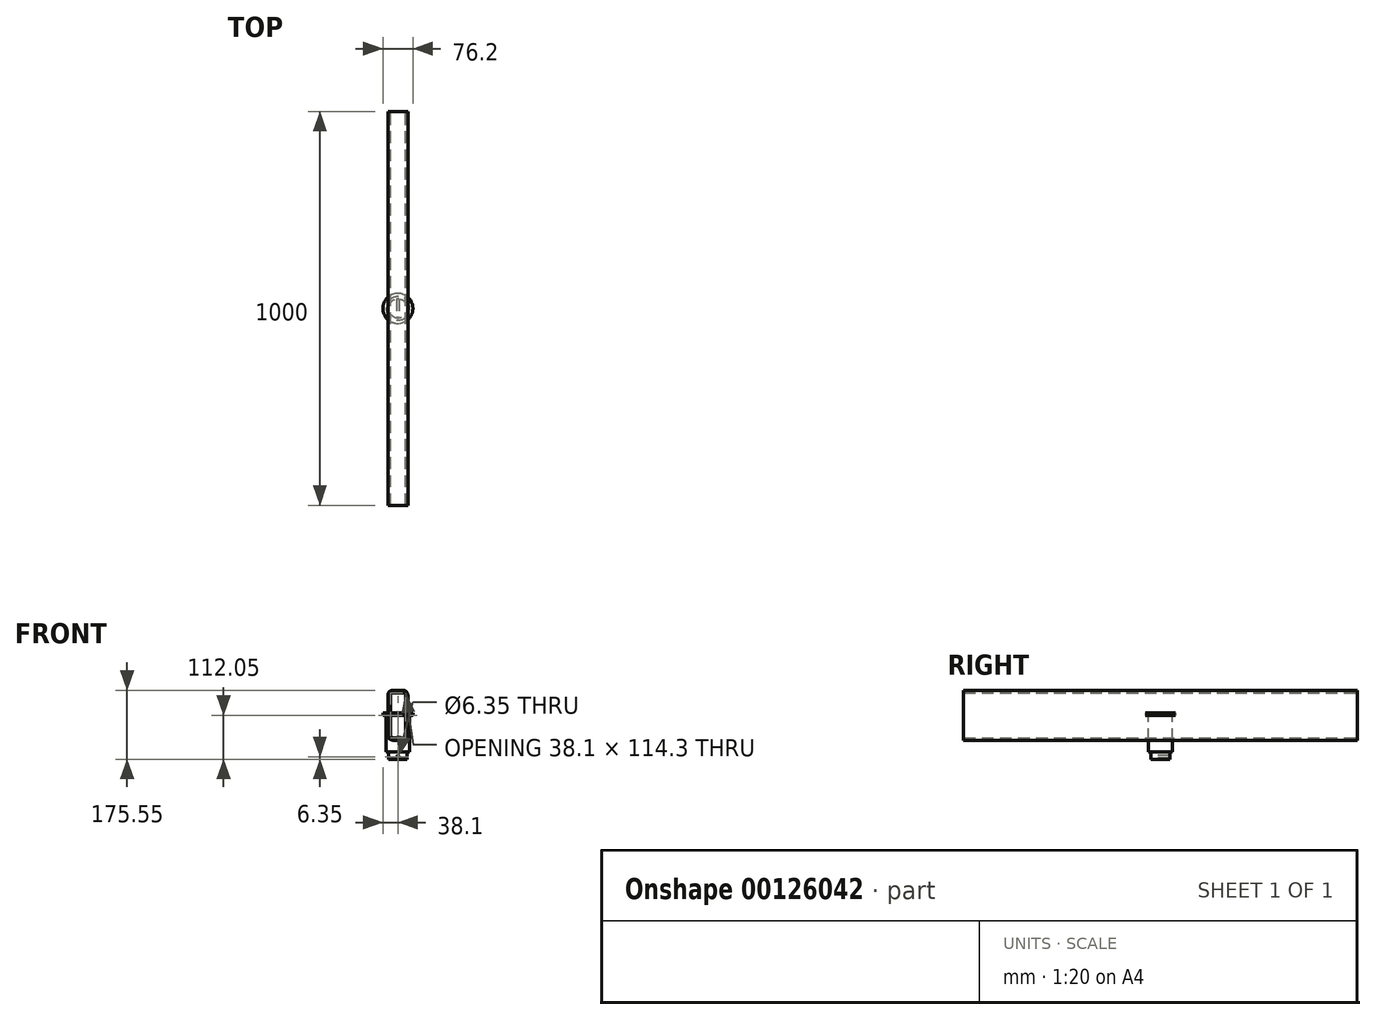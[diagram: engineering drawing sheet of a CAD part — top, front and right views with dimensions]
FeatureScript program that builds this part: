
annotation { "Feature Type Name" : "Feature", "Feature Type Description" : "" }
export const myFeature = defineFeature(function(context is Context, id is Id, definition is map)
    precondition{}
    {
        {
            var Q0;
            Q0=qCreatedBy(makeId("Top.planeOp"),FACE);
            var sketch = newSketch(context, id + "F0", { "sketchPlane" : qUnion([Q0])});
            skCircle(sketch, "E0", {"center": v(0, 0) * mm, "radius": 30 * mm});
            skSolve(sketch);
        }
        {
            var Q0;
            Q0 = qSketchRegion(id + "F0", true);
            extrude(context, id + "F1", {"entities" : qUnion([Q0]), "oppositeDirection" : true, "depth" : 93 * mm});
        }
        {
            var Q0;
            Q0=makeQuery(id+"F1.opExtrude","CAP_FACE",FACE,{"disambiguationData":[OSD([sQuery(id+"F0.wireOp",EDGE,"E0")])],"isStart":true});
            var sketch = newSketch(context, id + "F2", { "sketchPlane" : qUnion([Q0])});
            skCircle(sketch, "E1", {"center": v(0, 0) * mm, "radius": 38.1 * mm});
            skSolve(sketch);
        }
        {
            var Q0;
            Q0 = qSketchRegion(id + "F2", true);
            extrude(context, id + "F3", {"entities" : qUnion([Q0]), "operationType" : NewBodyOperationType.ADD, "depth" : 6.35 * mm});
        }
        {
            var Q0;
            Q0=makeQuery(id+"F1.opExtrude","CAP_FACE",FACE,{"disambiguationData":[OSD([sQuery(id+"F0.wireOp",EDGE,"E0")])],"isStart":false});
            var sketch = newSketch(context, id + "F4", { "sketchPlane" : qUnion([Q0])});
            skCircle(sketch, "E2", {"center": v(0, 0) * mm, "radius": 23.75 * mm});
            skSolve(sketch);
        }
        {
            var Q0;
            Q0=makeQuery(id+"F4.imprint","IMPRINT",FACE,{"disambiguationData":[TD([[makeQuery(id+"F4.imprint","IMPRINT",EDGE,{"derivedFrom":sQuery(id+"F4.wireOp",EDGE,"E2")}),1.0]])]});
            var Q1;
            Q1=sQuery(id+"F4.wireOp",EDGE,"E2");
            extrude(context, id + "F5", {"entities" : qUnion([Q0]), "surfaceEntities" : qUnion([Q1]), "depth" : 19.05 * mm});
        }
        {
            var Q0;
            Q0=qCreatedBy(makeId("Front.planeOp"),FACE);
            var sketch = newSketch(context, id + "F6", { "sketchPlane" : qUnion([Q0])});
            skCircle(sketch, "E3", {"center": v(0, -105.7) * mm, "radius": 3.17 * mm});
            skSolve(sketch);
        }
        {
            var Q0;
            Q0 = qSketchRegion(id + "F6", true);
            extrude(context, id + "F7", {"entities" : qUnion([Q0]), "operationType" : NewBodyOperationType.REMOVE, "endBound" : BoundingType.SYMMETRIC, "oppositeDirection" : true, "depth" : 60 * mm});
        }
        {
            var Q0;
            Q0=makeQuery(id+"F5.opExtrude","SWEPT_BODY",BODY,{"disambiguationData":[OSD([sQuery(id+"F4.wireOp",EDGE,"E2")])]});
            deleteBodies(context, id + "F8", {"entities" : qUnion([Q0])});
        }
        {
            var Q0;
            Q0=makeQuery(id+"F1.opExtrude","CAP_FACE",FACE,{"disambiguationData":[OSD([sQuery(id+"F0.wireOp",EDGE,"E0")])],"isStart":false});
            var sketch = newSketch(context, id + "F9", { "sketchPlane" : qUnion([Q0])});
            skCircle(sketch, "E4", {"center": v(0, 0) * mm, "radius": 23.75 * mm});
            skSolve(sketch);
        }
        {
            var Q0;
            Q0=makeQuery(id+"F9.imprint","IMPRINT",FACE,{"disambiguationData":[TD([[makeQuery(id+"F9.imprint","IMPRINT",EDGE,{"derivedFrom":sQuery(id+"F9.wireOp",EDGE,"E4")}),1.0]])]});
            extrude(context, id + "F10", {"entities" : qUnion([Q0]), "operationType" : NewBodyOperationType.ADD, "depth" : 19.05 * mm});
        }
        {
            var Q0;
            Q0=qCreatedBy(makeId("Front.planeOp"),FACE);
            var sketch = newSketch(context, id + "F11", { "sketchPlane" : qUnion([Q0])});
            skCircle(sketch, "E5", {"center": v(0, -105.7) * mm, "radius": 3.18 * mm});
            skSolve(sketch);
        }
        {
            var Q0;
            Q0 = qSketchRegion(id + "F11", true);
            extrude(context, id + "F12", {"entities" : qUnion([Q0]), "operationType" : NewBodyOperationType.REMOVE, "endBound" : BoundingType.SYMMETRIC, "oppositeDirection" : true, "depth" : 60 * mm});
        }
        {
            var Q0;
            Q0=qCreatedBy(makeId("Front.planeOp"),FACE);
            var sketch = newSketch(context, id + "F13", { "sketchPlane" : qUnion([Q0])});
            skLineSegment(sketch, "E6.bottom", {"start": v(12.7, 63.5) * mm, "end": v(-12.7, 63.5) * mm});
            skLineSegment(sketch, "E6.top", {"start": v(12.7, -63.5) * mm, "end": v(-12.7, -63.5) * mm});
            skLineSegment(sketch, "E6.left", {"start": v(25.4, 50.8) * mm, "end": v(25.4, -50.8) * mm});
            skLineSegment(sketch, "E6.right", {"start": v(-25.4, 50.8) * mm, "end": v(-25.4, -50.8) * mm});
            skPoint(sketch, "E6.middle", {"position": v(0, 0) * mm});
            skPoint(sketch, "E7.visualSharp", {"position": v(-25.4, 63.5) * mm});
            skArc(sketch, "E7.filletArc", {"start": v(-12.7, 63.5) * mm, "mid": v(-21.68, 59.78) * mm, "end": v(-25.4, 50.8) * mm});
            skPoint(sketch, "E8.visualSharp", {"position": v(25.4, 63.5) * mm});
            skArc(sketch, "E8.filletArc", {"start": v(25.4, 50.8) * mm, "mid": v(21.68, 59.78) * mm, "end": v(12.7, 63.5) * mm});
            skPoint(sketch, "E9.visualSharp", {"position": v(25.4, -63.5) * mm});
            skArc(sketch, "E9.filletArc", {"start": v(12.7, -63.5) * mm, "mid": v(21.68, -59.78) * mm, "end": v(25.4, -50.8) * mm});
            skPoint(sketch, "E10.visualSharp", {"position": v(-25.4, -63.5) * mm});
            skArc(sketch, "E10.filletArc", {"start": v(-25.4, -50.8) * mm, "mid": v(-21.68, -59.78) * mm, "end": v(-12.7, -63.5) * mm});
            skLineSegment(sketch, "E11.0", {"start": v(12.7, 57.15) * mm, "end": v(-12.7, 57.15) * mm});
            skArc(sketch, "E12.0", {"start": v(19.05, 50.8) * mm, "mid": v(17.2, 55.3) * mm, "end": v(12.7, 57.15) * mm});
            skLineSegment(sketch, "E13.0", {"start": v(19.05, 50.8) * mm, "end": v(19.05, -50.8) * mm});
            skArc(sketch, "E14.0", {"start": v(-12.7, 57.15) * mm, "mid": v(-17.2, 55.3) * mm, "end": v(-19.05, 50.8) * mm});
            skArc(sketch, "E14.1", {"start": v(12.7, -57.15) * mm, "mid": v(17.2, -55.3) * mm, "end": v(19.05, -50.8) * mm});
            skLineSegment(sketch, "E14.2", {"start": v(12.7, -57.15) * mm, "end": v(-12.7, -57.15) * mm});
            skArc(sketch, "E14.3", {"start": v(-19.05, -50.8) * mm, "mid": v(-17.2, -55.3) * mm, "end": v(-12.7, -57.15) * mm});
            skLineSegment(sketch, "E14.4", {"start": v(-19.05, 50.8) * mm, "end": v(-19.05, -50.8) * mm});
            skSolve(sketch);
        }
        {
            var Q0;
            Q0=makeQuery(id+"F13.imprint","IMPRINT",FACE,{"disambiguationData":[TD([[makeQuery(id+"F13.imprint","IMPRINT",EDGE,{"derivedFrom":sQuery(id+"F13.wireOp",EDGE,"E6.bottom")}),1.0]])]});
            extrude(context, id + "F14", {"entities" : qUnion([Q0]), "endBound" : BoundingType.SYMMETRIC, "depth" : 1000 * mm});
        }
    });
